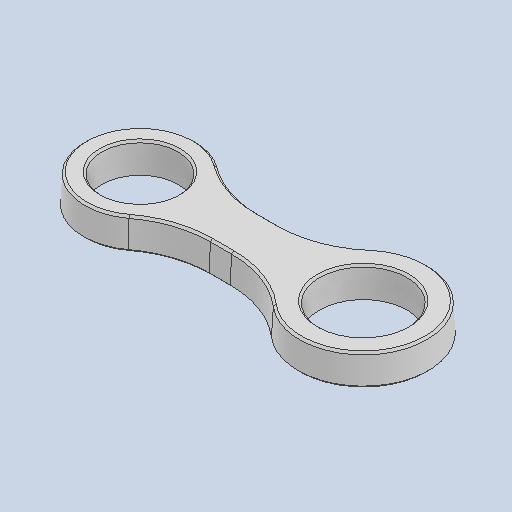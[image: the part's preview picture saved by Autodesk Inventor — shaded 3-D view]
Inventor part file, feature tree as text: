
AUTODESK INVENTOR PART (.ipt)
format: ipt  version: 2023 (Build 270158000, 158)  size: 319,488 bytes
history: native  units: in
note: dims shown in document units (in); Inventor stores cm internally (conversion verified against a paired STEP export)
features: chamfer x2, extrude x1, fillet x1, draft x1, sketch x1
ambient origin geometry x8: Origin, YZ Plane, XZ Plane, XY Plane, X Axis, Y Axis, Z Axis, Center Point
bodies: Body1 (feature_tree)
feature tree (6):
  extrude  "Extrusion2"  Depth=1.0in
  fillet  "Fillet3"  Radius=1.3in
  draft  "FaceDraft2"
  chamfer  "Chamfer1"  Distance=0.76in
  chamfer  "Chamfer2"  Distance=1.125in
  sketch  "Sketch1"  dims[d15=0.872in d17=0.5in d18=1.3in d19=0.76in d20=1.125in d21=2.225in d22=0.3in d23=0.0in d27=1.0in d28=0.0206in d29=0.02in d30=0.125in d31=45.0deg d32=0.02in d33=0.125in d34=45.0deg d3=0.5in d4=0.0344in d5=0.5in d6=0.0344in]
